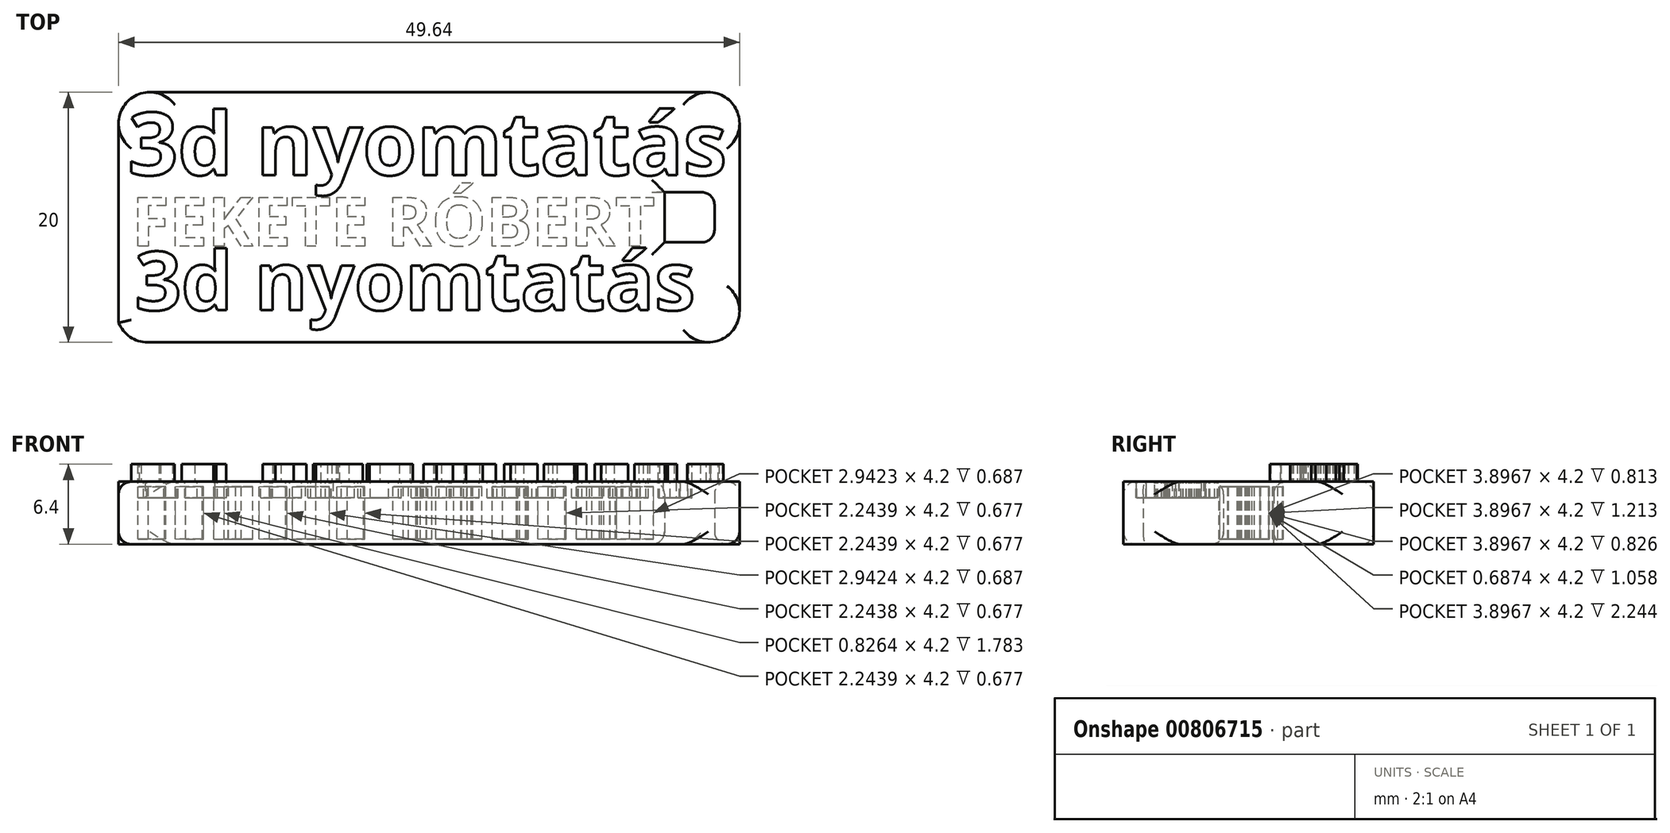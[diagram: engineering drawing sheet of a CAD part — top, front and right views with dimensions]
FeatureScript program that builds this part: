
annotation { "Feature Type Name" : "Feature", "Feature Type Description" : "" }
export const myFeature = defineFeature(function(context is Context, id is Id, definition is map)
    precondition{}
    {
        {
            var Q0;
            Q0=qCreatedBy(makeId("Top.planeOp"),FACE);
            var sketch = newSketch(context, id + "F0", { "sketchPlane" : qUnion([Q0])});
            skLineSegment(sketch, "E0.bottom", {"start": v(22.32, -10) * mm, "end": v(-22.5, -10) * mm});
            skLineSegment(sketch, "E0.top", {"start": v(22.32, 10) * mm, "end": v(-22.32, 10) * mm});
            skLineSegment(sketch, "E0.left", {"start": v(24.82, -7.5) * mm, "end": v(24.82, 7.5) * mm});
            skLineSegment(sketch, "E0.right", {"start": v(-24.82, -8.43) * mm, "end": v(-24.82, 7.5) * mm});
            skPoint(sketch, "E0.middle", {"position": v(0, 0) * mm});
            skArc(sketch, "E1", {"start": v(24.82, 7.5) * mm, "mid": v(24.09, 9.27) * mm, "end": v(22.32, 10) * mm});
            skPoint(sketch, "E2.startSnap0", {"position": v(0, 10) * mm});
            skArc(sketch, "E3.MirrorC", {"start": v(-24.82, 7.5) * mm, "mid": v(-24.09, 9.27) * mm, "end": v(-22.32, 10) * mm});
            skArc(sketch, "E4.MirrorC", {"start": v(24.82, -7.5) * mm, "mid": v(24.09, -9.27) * mm, "end": v(22.32, -10) * mm});
            skArc(sketch, "E5.MirrorC", {"start": v(-24.82, -8.43) * mm, "mid": v(-23.9, -9.57) * mm, "end": v(-22.5, -10) * mm});
            skPoint(sketch, "E6.orphan", {"position": v(-24.82, 10) * mm});
            skLineSegment(sketch, "E7.bottom", {"start": v(22.82, -2) * mm, "end": v(18.82, -2) * mm});
            skLineSegment(sketch, "E7.top", {"start": v(22.82, 2) * mm, "end": v(18.82, 2) * mm});
            skLineSegment(sketch, "E7.left", {"start": v(22.82, -2) * mm, "end": v(22.82, 2) * mm});
            skLineSegment(sketch, "E7.right", {"start": v(18.82, -2) * mm, "end": v(18.82, 2) * mm});
            skPoint(sketch, "E7.middle", {"position": v(20.82, 0) * mm});
            skPoint(sketch, "E8.orphan", {"position": v(24.82, 10) * mm});
            skPoint(sketch, "E9.orphan", {"position": v(24.82, -10) * mm});
            skPoint(sketch, "E10.orphan", {"position": v(-24.82, -10) * mm});
            skSolve(sketch);
        }
        {
            var Q0;
            Q0=makeQuery(id+"F0.imprint","IMPRINT",FACE,{"disambiguationData":[TD([[makeQuery(id+"F0.imprint","IMPRINT",EDGE,{"derivedFrom":sQuery(id+"F0.wireOp",EDGE,"E0.bottom")}),-1.0]])]});
            extrude(context, id + "F1", {"entities" : qUnion([Q0]), "depth" : 5 * mm, "offsetDistance" : 25 * mm});
        }
        {
            var Q0;
            Q0=makeQuery(id+"F1.opExtrude","CAP_FACE",FACE,{"disambiguationData":[OSD([sQuery(id+"F0.wireOp",EDGE,"E0.bottom"),sQuery(id+"F0.wireOp",EDGE,"E0.top"),sQuery(id+"F0.wireOp",EDGE,"E0.left"),sQuery(id+"F0.wireOp",EDGE,"E0.right"),sQuery(id+"F0.wireOp",EDGE,"E1"),sQuery(id+"F0.wireOp",EDGE,"E3.MirrorC"),sQuery(id+"F0.wireOp",EDGE,"E4.MirrorC"),sQuery(id+"F0.wireOp",EDGE,"E5.MirrorC"),sQuery(id+"F0.wireOp",EDGE,"E7.bottom"),sQuery(id+"F0.wireOp",EDGE,"E7.top"),sQuery(id+"F0.wireOp",EDGE,"E7.left"),sQuery(id+"F0.wireOp",EDGE,"E7.right")])],"isStart":false});
            var sketch = newSketch(context, id + "F2", { "sketchPlane" : qUnion([Q0])});
            skText(sketch, "E11", { "text": "3d nyomtatás", "fontName": "OpenSans-Bold.ttf"});
            const initialGuessF2  = {"E11": [-0.02406, 0.00338, 1, 0, 0.00502]};
            skSetInitialGuess(sketch, initialGuessF2);
            skSolve(sketch);
        }
        {
            var Q0;
            Q0=makeQuery(id+"F2.imprint","IMPRINT",FACE,{"disambiguationData":[TD([[makeQuery(id+"F2.imprint","IMPRINT",EDGE,{"derivedFrom":sQuery(id+"F2.wireOp",EDGE,"E11.sketch_text.stroke-0")}),1.0]])]});
            var sketch = newSketch(context, id + "F3", { "sketchPlane" : qUnion([Q0])});
            skText(sketch, "E12", { "text": "3d nyomtatás", "fontName": "OpenSans-Bold.ttf"});
            const initialGuessF3  = {"E12": [-0.02353, -0.00743, 1, 0, 0.0047]};
            skSetInitialGuess(sketch, initialGuessF3);
            skSolve(sketch);
        }
        {
            var Q0;
            Q0=makeQuery(id+"F2.imprint","IMPRINT",FACE,{"disambiguationData":[TD([[makeQuery(id+"F2.imprint","IMPRINT",EDGE,{"derivedFrom":sQuery(id+"F2.wireOp",EDGE,"E11.sketch_text.stroke-0")}),1.0]])]});
            var sketch = newSketch(context, id + "F4", { "sketchPlane" : qUnion([Q0])});
            skText(sketch, "E13", { "text": "FEKETE RÓBERT", "fontName": "OpenSans-Bold.ttf"});
            const initialGuessF4  = {"E13": [-0.02376, -0.0023, 1, 0, 0.00393]};
            skSetInitialGuess(sketch, initialGuessF4);
            skSolve(sketch);
        }
        {
            var Q0;
            Q0 = qSketchRegion(id + "F4", true);
            extrude(context, id + "F5", {"entities" : qUnion([Q0]), "operationType" : NewBodyOperationType.REMOVE, "oppositeDirection" : true, "depth" : 4.6 * mm, "offsetDistance" : 25 * mm, "hasSecondDirection" : true, "secondDirectionOppositeDirection" : true, "secondDirectionDepth" : .4 * mm});
        }
        {
            var Q0;
            Q0 = qSketchRegion(id + "F2", true);
            extrude(context, id + "F6", {"entities" : qUnion([Q0]), "operationType" : NewBodyOperationType.ADD, "depth" : 1.4 * mm, "offsetDistance" : 25 * mm});
        }
        {
            var Q0;
            Q0 = qSketchRegion(id + "F3", true);
            extrude(context, id + "F7", {"entities" : qUnion([Q0]), "operationType" : NewBodyOperationType.REMOVE, "oppositeDirection" : true, "depth" : 1.3 * mm, "offsetDistance" : 25 * mm});
        }
        {
            var Q0;
            Q0=makeQuery(id+"F1.opExtrude","CAP_EDGE",EDGE,{"disambiguationData":[OSD([sQuery(id+"F0.wireOp",EDGE,"E0.right")])],"isStart":false});
            var Q1;
            Q1=makeQuery(id+"F1.opExtrude","CAP_EDGE",EDGE,{"disambiguationData":[OSD([sQuery(id+"F0.wireOp",EDGE,"E0.top")])],"isStart":false});
            var Q2;
            Q2=makeQuery(id+"F1.opExtrude","CAP_EDGE",EDGE,{"disambiguationData":[OSD([sQuery(id+"F0.wireOp",EDGE,"E0.bottom")])],"isStart":false});
            var Q3;
            Q3=makeQuery(id+"F1.opExtrude","CAP_EDGE",EDGE,{"disambiguationData":[OSD([sQuery(id+"F0.wireOp",EDGE,"E0.left")])],"isStart":false});
            var Q4;
            Q4=makeQuery(id+"F1.opExtrude","CAP_EDGE",EDGE,{"disambiguationData":[OSD([sQuery(id+"F0.wireOp",EDGE,"E0.right")])],"isStart":true});
            var Q5;
            Q5=makeQuery(id+"F1.opExtrude","CAP_EDGE",EDGE,{"disambiguationData":[OSD([sQuery(id+"F0.wireOp",EDGE,"E0.bottom")])],"isStart":true});
            var Q6;
            Q6=makeQuery(id+"F1.opExtrude","CAP_EDGE",EDGE,{"disambiguationData":[OSD([sQuery(id+"F0.wireOp",EDGE,"E0.left")])],"isStart":true});
            var Q7;
            Q7=makeQuery(id+"F1.opExtrude","CAP_EDGE",EDGE,{"disambiguationData":[OSD([sQuery(id+"F0.wireOp",EDGE,"E0.top")])],"isStart":true});
            var Q8;
            Q8=makeQuery(id+"F1.opExtrude","CAP_EDGE",EDGE,{"disambiguationData":[OSD([sQuery(id+"F0.wireOp",EDGE,"E7.top")])],"isStart":false});
            var Q9;
            Q9=makeQuery(id+"F1.opExtrude","CAP_EDGE",EDGE,{"disambiguationData":[OSD([sQuery(id+"F0.wireOp",EDGE,"E7.left")])],"isStart":false});
            var Q10;
            Q10=makeQuery(id+"F1.opExtrude","CAP_EDGE",EDGE,{"disambiguationData":[OSD([sQuery(id+"F0.wireOp",EDGE,"E7.right")])],"isStart":true});
            var Q11;
            Q11=makeQuery(id+"F1.opExtrude","CAP_EDGE",EDGE,{"disambiguationData":[OSD([sQuery(id+"F0.wireOp",EDGE,"E7.bottom")])],"isStart":false});
            var Q12;
            Q12=makeQuery(id+"F1.opExtrude","CAP_EDGE",EDGE,{"disambiguationData":[OSD([sQuery(id+"F0.wireOp",EDGE,"E7.bottom")])],"isStart":true});
            var Q13;
            Q13=makeQuery(id+"F1.opExtrude","SWEPT_FACE",FACE,{"disambiguationData":[OSD([sQuery(id+"F0.wireOp",EDGE,"E7.left")])]});
            var Q14;
            Q14=makeQuery(id+"F1.opExtrude","CAP_EDGE",EDGE,{"disambiguationData":[OSD([sQuery(id+"F0.wireOp",EDGE,"E7.right")])],"isStart":false});
            fillet(context, id + "F8", {"entities" : qUnion([Q0, Q1, Q2, Q3, Q4, Q5, Q6, Q7, Q8, Q9, Q10, Q11, Q12, Q13, Q14]), "radius" : 1 * mm, "tangentPropagation" : true, "allowEdgeOverflow" : false});
        }
    });
